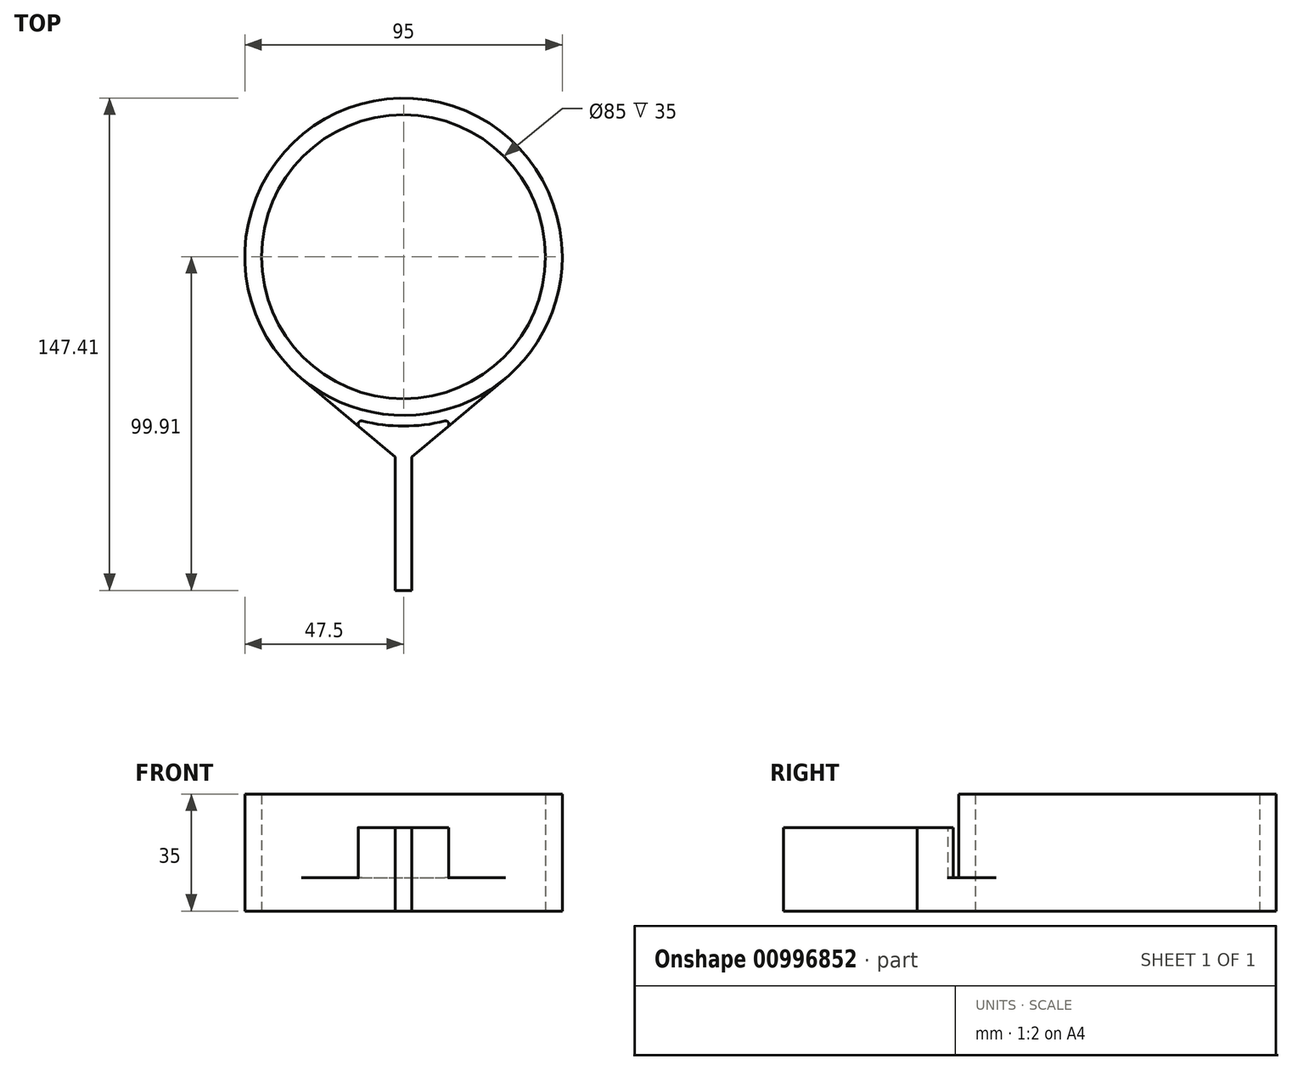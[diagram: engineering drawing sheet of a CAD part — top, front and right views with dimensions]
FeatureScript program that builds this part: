
annotation { "Feature Type Name" : "Feature", "Feature Type Description" : "" }
export const myFeature = defineFeature(function(context is Context, id is Id, definition is map)
    precondition{}
    {
        {
            var Q0;
            Q0=qCreatedBy(makeId("Top.planeOp"),FACE);
            var sketch = newSketch(context, id + "F0", { "sketchPlane" : qUnion([Q0])});
            skCircle(sketch, "E0", {"center": v(0, 0) * mm, "radius": 47.5 * mm});
            skCircle(sketch, "E1", {"center": v(0, 0) * mm, "radius": 42.5 * mm});
            skSolve(sketch);
        }
        {
            var Q0;
            Q0 = qSketchRegion(id + "F0", true);
            extrude(context, id + "F1", {"entities" : qUnion([Q0]), "depth" : 35 * mm, "offsetDistance" : 25 * mm});
        }
        {
            var Q0;
            Q0=qCreatedBy(makeId("Top.planeOp"),FACE);
            var Q1;
            Q1=qCreatedBy(makeId("Top.planeOp"),FACE);
            var sketch = newSketch(context, id + "F2", { "sketchPlane" : qUnion([Q0, Q1])});
            skLineSegment(sketch, "E2", {"start": v(0, 0) * mm, "end": v(-30.53, -36.39) * mm, "construction": true});
            skLineSegment(sketch, "E3", {"start": v(-30.53, -36.39) * mm, "end": v(-2.5, -59.9) * mm});
            skLineSegment(sketch, "E4", {"start": v(-2.5, -59.9) * mm, "end": v(-2.5, -99.9) * mm});
            skLineSegment(sketch, "E5", {"start": v(0, 0) * mm, "end": v(0, -99.9) * mm, "construction": true});
            skLineSegment(sketch, "E6", {"start": v(0, -99.9) * mm, "end": v(-2.5, -99.9) * mm});
            skLineSegment(sketch, "E7", {"start": v(-30.53, -36.39) * mm, "end": v(0, -47.5) * mm});
            skLineSegment(sketch, "E8.MirrorCS", {"start": v(30.53, -36.39) * mm, "end": v(0, -47.5) * mm});
            skLineSegment(sketch, "E9.MirrorCS", {"start": v(30.53, -36.39) * mm, "end": v(2.5, -59.9) * mm});
            skLineSegment(sketch, "E10.MirrorCS", {"start": v(2.5, -59.9) * mm, "end": v(2.5, -99.9) * mm});
            skLineSegment(sketch, "E11.MirrorCS", {"start": v(0, -99.9) * mm, "end": v(2.5, -99.9) * mm});
            skSolve(sketch);
        }
        {
            var Q0;
            Q0 = qSketchRegion(id + "F2", true);
            extrude(context, id + "F3", {"entities" : qUnion([Q0]), "operationType" : NewBodyOperationType.ADD, "depth" : 25 * mm, "offsetDistance" : 25 * mm});
        }
        {
            var Q0;
            Q0=makeQuery(id+"F1.opExtrude","CAP_FACE",FACE,{"disambiguationData":[OSD([sQuery(id+"F0.wireOp",EDGE,"E0"),sQuery(id+"F0.wireOp",EDGE,"E1")])],"isStart":false});
            var Q1;
            Q1=makeQuery(id+"F1.opExtrude","CAP_FACE",FACE,{"disambiguationData":[OSD([sQuery(id+"F0.wireOp",EDGE,"E0"),sQuery(id+"F0.wireOp",EDGE,"E1")])],"isStart":false});
            var sketch = newSketch(context, id + "F4", { "sketchPlane" : qUnion([Q0, Q1])});
            skArc(sketch, "E12", {"start": v(-30.53, -36.39) * mm, "mid": v(0, -47.5) * mm, "end": v(30.53, -36.39) * mm});
            skArc(sketch, "E13.0", {"start": v(-32.59, -38.84) * mm, "mid": v(0, -50.7) * mm, "end": v(32.59, -38.84) * mm});
            skLineSegment(sketch, "E14", {"start": v(-30.53, -36.39) * mm, "end": v(-32.59, -38.84) * mm});
            skLineSegment(sketch, "E15", {"start": v(30.53, -36.39) * mm, "end": v(32.59, -38.84) * mm});
            skSolve(sketch);
        }
        {
            var Q0;
            Q0 = qSketchRegion(id + "F4", true);
            extrude(context, id + "F5", {"entities" : qUnion([Q0]), "operationType" : NewBodyOperationType.REMOVE, "oppositeDirection" : true, "depth" : 25 * mm, "offsetDistance" : 25 * mm});
        }
        {
            var Q0;
            Q0=makeQuery(id+"F5.boolean.opBoolean","INTERSECT",EDGE,{"derivedFrom":[makeQuery(id+"F3.opExtrude","SWEPT_FACE",FACE,{"disambiguationData":[OSD([sQuery(id+"F2.wireOp",EDGE,"E9.MirrorCS")])]}),makeQuery(id+"F5.opExtrude","SWEPT_FACE",FACE,{"disambiguationData":[OSD([sQuery(id+"F4.wireOp",EDGE,"E13.0")])]})]});
            var Q1;
            Q1=makeQuery(id+"F5.boolean.opBoolean","INTERSECT",EDGE,{"derivedFrom":[makeQuery(id+"F3.opExtrude","SWEPT_FACE",FACE,{"disambiguationData":[OSD([sQuery(id+"F2.wireOp",EDGE,"E3")])]}),makeQuery(id+"F5.opExtrude","SWEPT_FACE",FACE,{"disambiguationData":[OSD([sQuery(id+"F4.wireOp",EDGE,"E13.0")])]})]});
            fillet(context, id + "F6", {"entities" : qUnion([Q0, Q1]), "radius" : 1 * mm, "tangentPropagation" : true, "allowEdgeOverflow" : false});
        }
    });
